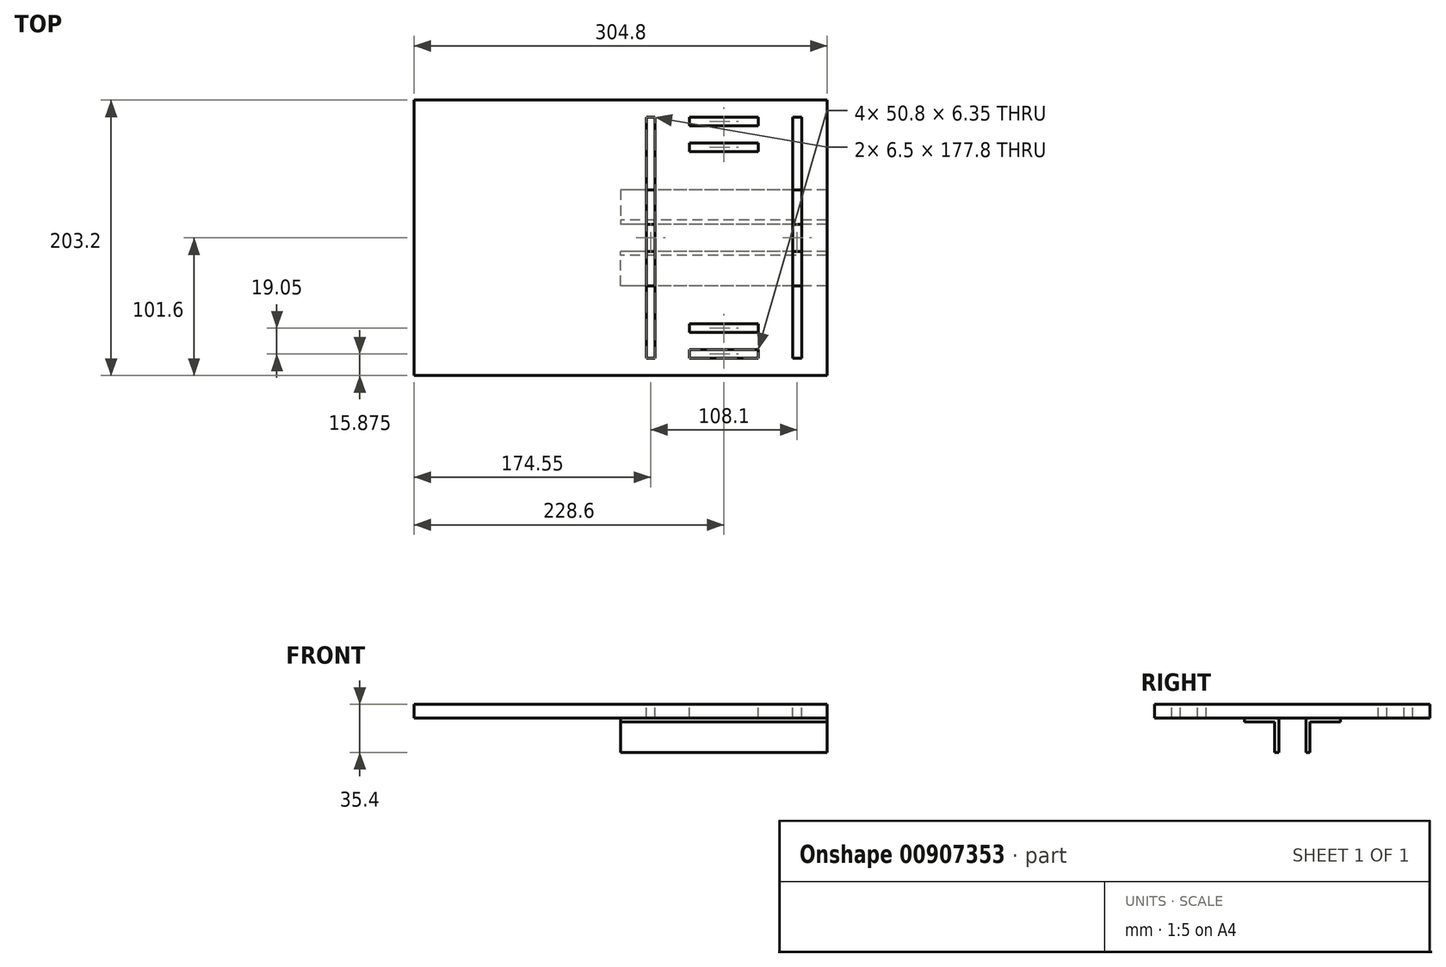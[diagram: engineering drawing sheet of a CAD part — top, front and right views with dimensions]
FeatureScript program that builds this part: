
annotation { "Feature Type Name" : "Feature", "Feature Type Description" : "" }
export const myFeature = defineFeature(function(context is Context, id is Id, definition is map)
    precondition{}
    {
        {
            var Q0;
            Q0=qCreatedBy(makeId("Top.planeOp"),FACE);
            var sketch = newSketch(context, id + "F0", { "sketchPlane" : qUnion([Q0])});
            skLineSegment(sketch, "E0.bottom", {"start": v(-152.4, 101.6) * mm, "end": v(152.4, 101.6) * mm});
            skLineSegment(sketch, "E0.top", {"start": v(-152.4, -101.6) * mm, "end": v(152.4, -101.6) * mm});
            skLineSegment(sketch, "E0.left", {"start": v(-152.4, 101.6) * mm, "end": v(-152.4, -101.6) * mm});
            skLineSegment(sketch, "E0.right", {"start": v(152.4, 101.6) * mm, "end": v(152.4, -101.6) * mm});
            skSolve(sketch);
        }
        {
            var Q0;
            Q0=makeQuery(id+"F0.imprint","IMPRINT",FACE,{"disambiguationData":[TD([[makeQuery(id+"F0.imprint","IMPRINT",EDGE,{"derivedFrom":sQuery(id+"F0.wireOp",EDGE,"E0.bottom")}),-1.0]])]});
            extrude(context, id + "F1", {"entities" : qUnion([Q0]), "depth" : 10 * mm, "offsetDistance" : 25 * mm});
        }
        {
            var Q0;
            Q0=makeQuery(id+"F1.opExtrude","CAP_FACE",FACE,{"disambiguationData":[OSD([sQuery(id+"F0.wireOp",EDGE,"E0.bottom"),sQuery(id+"F0.wireOp",EDGE,"E0.top"),sQuery(id+"F0.wireOp",EDGE,"E0.left"),sQuery(id+"F0.wireOp",EDGE,"E0.right")])],"isStart":false});
            var sketch = newSketch(context, id + "F2", { "sketchPlane" : qUnion([Q0])});
            skLineSegment(sketch, "E1.bottom", {"start": v(50.8, 88.9) * mm, "end": v(101.6, 88.9) * mm});
            skLineSegment(sketch, "E1.top", {"start": v(50.8, 82.55) * mm, "end": v(101.6, 82.55) * mm});
            skLineSegment(sketch, "E1.left", {"start": v(50.8, 88.9) * mm, "end": v(50.8, 82.55) * mm});
            skLineSegment(sketch, "E1.right", {"start": v(101.6, 88.9) * mm, "end": v(101.6, 82.55) * mm});
            skLineSegment(sketch, "E2.bottom", {"start": v(50.8, 69.85) * mm, "end": v(101.6, 69.85) * mm});
            skLineSegment(sketch, "E2.top", {"start": v(50.8, 63.5) * mm, "end": v(101.6, 63.5) * mm});
            skLineSegment(sketch, "E2.left", {"start": v(50.8, 69.85) * mm, "end": v(50.8, 63.5) * mm});
            skLineSegment(sketch, "E2.right", {"start": v(101.6, 69.85) * mm, "end": v(101.6, 63.5) * mm});
            skLineSegment(sketch, "E3.MirrorCS", {"start": v(50.8, -63.5) * mm, "end": v(101.6, -63.5) * mm});
            skLineSegment(sketch, "E4.MirrorCS", {"start": v(50.8, -69.85) * mm, "end": v(101.6, -69.85) * mm});
            skLineSegment(sketch, "E5.MirrorCS", {"start": v(50.8, -69.85) * mm, "end": v(50.8, -63.5) * mm});
            skLineSegment(sketch, "E6.MirrorCS", {"start": v(101.6, -69.85) * mm, "end": v(101.6, -63.5) * mm});
            skLineSegment(sketch, "E7.MirrorCS", {"start": v(50.8, -88.9) * mm, "end": v(101.6, -88.9) * mm});
            skLineSegment(sketch, "E8.MirrorCS", {"start": v(50.8, -82.55) * mm, "end": v(101.6, -82.55) * mm});
            skLineSegment(sketch, "E9.MirrorCS", {"start": v(101.6, -88.9) * mm, "end": v(101.6, -82.55) * mm});
            skLineSegment(sketch, "E10.MirrorCS", {"start": v(50.8, -88.9) * mm, "end": v(50.8, -82.55) * mm});
            skLineSegment(sketch, "E11.bottom", {"start": v(127, 88.9) * mm, "end": v(133.5, 88.9) * mm});
            skLineSegment(sketch, "E11.top", {"start": v(127, -88.9) * mm, "end": v(133.5, -88.9) * mm});
            skLineSegment(sketch, "E11.left", {"start": v(127, 88.9) * mm, "end": v(127, -88.9) * mm});
            skLineSegment(sketch, "E11.right", {"start": v(133.5, 88.9) * mm, "end": v(133.5, -88.9) * mm});
            skLineSegment(sketch, "E12.bottom", {"start": v(25.4, -88.9) * mm, "end": v(18.9, -88.9) * mm});
            skLineSegment(sketch, "E12.top", {"start": v(25.4, 88.9) * mm, "end": v(18.9, 88.9) * mm});
            skLineSegment(sketch, "E12.left", {"start": v(25.4, -88.9) * mm, "end": v(25.4, 88.9) * mm});
            skLineSegment(sketch, "E12.right", {"start": v(18.9, -88.9) * mm, "end": v(18.9, 88.9) * mm});
            skSolve(sketch);
        }
        {
            var Q0;
            Q0 = qSketchRegion(id + "F2", true);
            extrude(context, id + "F3", {"entities" : qUnion([Q0]), "operationType" : NewBodyOperationType.REMOVE, "oppositeDirection" : true, "depth" : 25 * mm, "offsetDistance" : 25 * mm});
        }
        {
            var Q0;
            Q0=qCreatedBy(makeId("Right.planeOp"),FACE);
            var sketch = newSketch(context, id + "F4", { "sketchPlane" : qUnion([Q0])});
            skLineSegment(sketch, "E13.top", {"start": v(-35.4, -3) * mm, "end": v(-13, -3) * mm});
            skLineSegment(sketch, "E13.left", {"start": v(-35.4, 0) * mm, "end": v(-35.4, -3) * mm});
            skLineSegment(sketch, "E13.right", {"start": v(-10, 0) * mm, "end": v(-10, -3) * mm});
            skLineSegment(sketch, "E14.top", {"start": v(-13, -25.4) * mm, "end": v(-10, -25.4) * mm});
            skLineSegment(sketch, "E14.left", {"start": v(-13, -3) * mm, "end": v(-13, -25.4) * mm});
            skLineSegment(sketch, "E14.right", {"start": v(-10, 0) * mm, "end": v(-10, -25.4) * mm});
            skLineSegment(sketch, "E15", {"start": v(-35.4, 0) * mm, "end": v(-10, 0) * mm});
            skSolve(sketch);
        }
        {
            var Q0;
            Q0=makeQuery(id+"F4.imprint","IMPRINT",FACE,{"disambiguationData":[TD([[makeQuery(id+"F4.imprint","IMPRINT",EDGE,{"derivedFrom":sQuery(id+"F4.wireOp",EDGE,"E13.top")}),1.0]])]});
            var Q1;
            Q1=makeQuery(id+"F1.opExtrude","SWEPT_FACE",FACE,{"disambiguationData":[OSD([sQuery(id+"F0.wireOp",EDGE,"E0.right")])]});
            extrude(context, id + "F5", {"entities" : qUnion([Q0]), "endBound" : BoundingType.UP_TO_SURFACE, "depth" : 25 * mm, "endBoundEntityFace" : qUnion([Q1]), "offsetDistance" : 25 * mm});
        }
        {
            var Q0;
            Q0=makeQuery(id+"F5.opExtrude","SWEPT_BODY",BODY,{"disambiguationData":[OSD([sQuery(id+"F4.wireOp",EDGE,"E13.top"),sQuery(id+"F4.wireOp",EDGE,"E13.left"),sQuery(id+"F4.wireOp",EDGE,"E14.top"),sQuery(id+"F4.wireOp",EDGE,"E14.left"),sQuery(id+"F4.wireOp",EDGE,"E14.right"),sQuery(id+"F4.wireOp",EDGE,"E15")])]});
            var Q1;
            Q1=qCreatedBy(makeId("Front.planeOp"),FACE);
            mirror(context, id + "F6", {"entities" : qUnion([Q0]), "mirrorPlane" : qUnion([Q1])});
        }
    });
